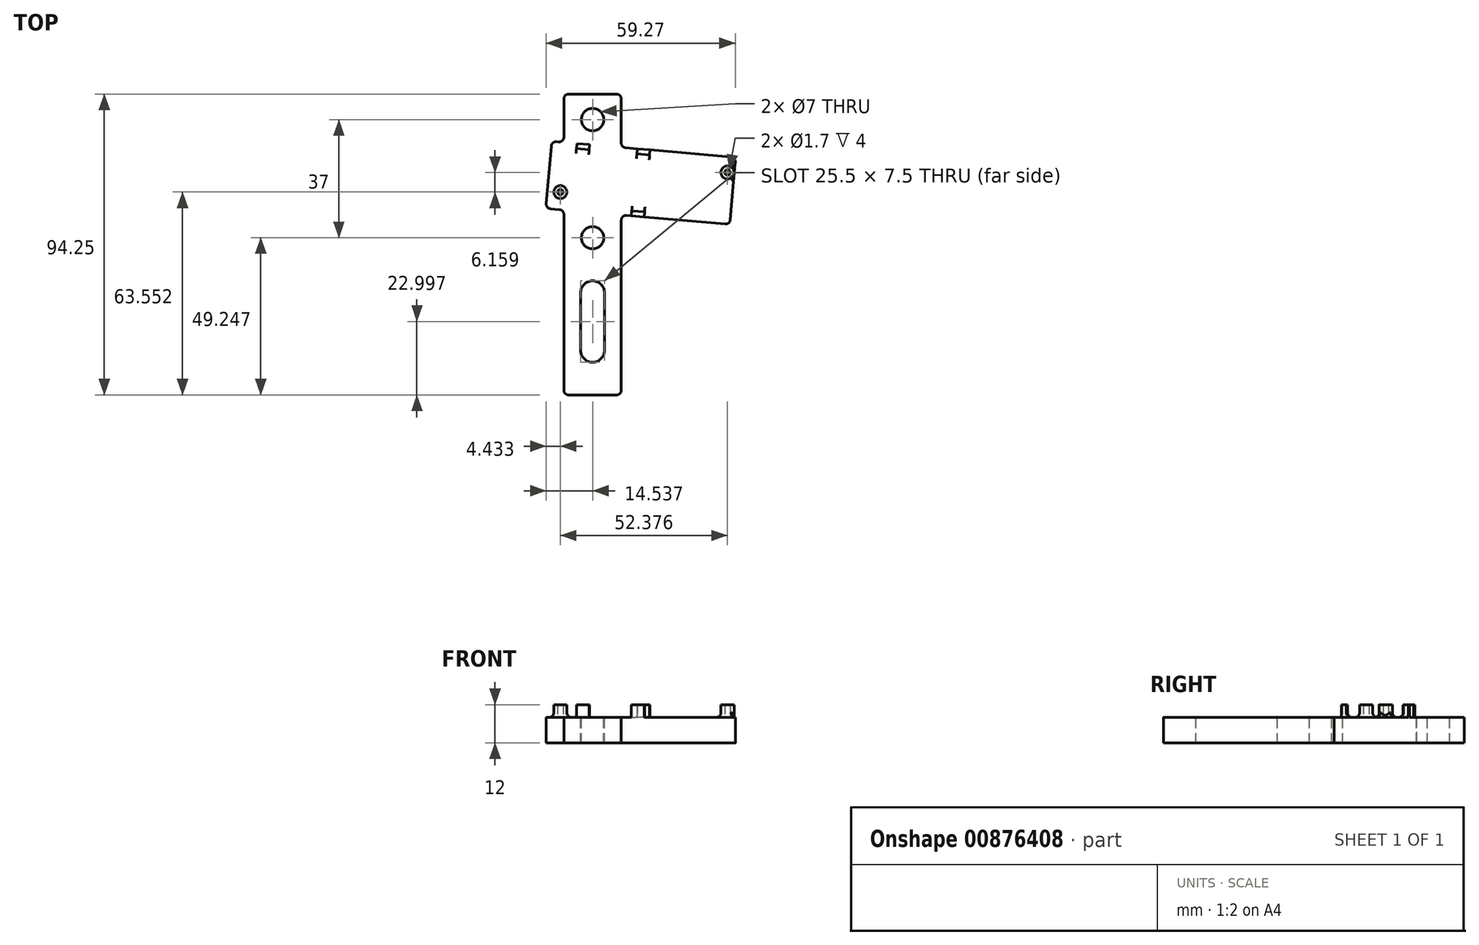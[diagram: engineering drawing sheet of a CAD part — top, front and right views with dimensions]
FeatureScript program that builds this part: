
annotation { "Feature Type Name" : "Feature", "Feature Type Description" : "" }
export const myFeature = defineFeature(function(context is Context, id is Id, definition is map)
    precondition{}
    {
        {
            var Q0;
            Q0=qCreatedBy(makeId("Top.planeOp"),FACE);
            var sketch = newSketch(context, id + "F0", { "sketchPlane" : qUnion([Q0])});
            skLineSegment(sketch, "E0", {"start": v(-42.89, -38.68) * mm, "end": v(35.48, -38.68) * mm, "construction": true});
            skCircle(sketch, "E1", {"center": v(-16.47, 2.12) * mm, "radius": 2.05 * mm});
            skCircle(sketch, "E2", {"center": v(35.9, 8.28) * mm, "radius": 2.05 * mm});
            skCircle(sketch, "E3", {"center": v(-16.47, 2.12) * mm, "radius": 0.85 * mm});
            skCircle(sketch, "E4", {"center": v(35.9, 8.28) * mm, "radius": 0.85 * mm});
            skLineSegment(sketch, "E5", {"start": v(-19.76, 11.54) * mm, "end": v(-9.28, 17.15) * mm, "construction": true});
            skLineSegment(sketch, "E6", {"start": v(-20.56, 2.34) * mm, "end": v(-11.12, -3.85) * mm, "construction": true});
            skLineSegment(sketch, "E7", {"start": v(28.2, -7.29) * mm, "end": v(37, -4.14) * mm, "construction": true});
            skLineSegment(sketch, "E8", {"start": v(-20.56, 2.34) * mm, "end": v(-21.03, -2.98) * mm, "construction": true});
            skLineSegment(sketch, "E9", {"start": v(-21.03, -2.98) * mm, "end": v(-11.12, -3.85) * mm, "construction": true});
            skLineSegment(sketch, "E10", {"start": v(-9.28, 17.15) * mm, "end": v(-19.2, 18.02) * mm, "construction": true});
            skLineSegment(sketch, "E11", {"start": v(-19.2, 18.02) * mm, "end": v(-19.76, 11.54) * mm, "construction": true});
            skLineSegment(sketch, "E12", {"start": v(37, -4.14) * mm, "end": v(36.66, -8.03) * mm, "construction": true});
            skLineSegment(sketch, "E13", {"start": v(36.66, -8.03) * mm, "end": v(28.2, -7.29) * mm, "construction": true});
            skLineSegment(sketch, "E14.bottom", {"start": v(11.5, 13.73) * mm, "end": v(11.65, 15.32) * mm});
            skLineSegment(sketch, "E14.top", {"start": v(7.52, 14.08) * mm, "end": v(7.66, 15.67) * mm});
            skLineSegment(sketch, "E14.left", {"start": v(11.5, 13.73) * mm, "end": v(7.52, 14.08) * mm});
            skLineSegment(sketch, "E14.right", {"start": v(11.65, 15.32) * mm, "end": v(7.66, 15.67) * mm});
            skLineSegment(sketch, "E15.bottom", {"start": v(9.76, -5.67) * mm, "end": v(9.9, -4.08) * mm});
            skLineSegment(sketch, "E15.top", {"start": v(5.78, -5.33) * mm, "end": v(5.92, -3.73) * mm});
            skLineSegment(sketch, "E15.left", {"start": v(9.76, -5.67) * mm, "end": v(5.78, -5.33) * mm});
            skLineSegment(sketch, "E15.right", {"start": v(9.9, -4.08) * mm, "end": v(5.92, -3.73) * mm});
            skPoint(sketch, "E16", {"position": v(9.65, 15.5) * mm});
            skPoint(sketch, "E17", {"position": v(7.82, -5.5) * mm});
            skPoint(sketch, "E18", {"position": v(-11.12, -3.85) * mm});
            skLineSegment(sketch, "E19.bottom", {"start": v(-11.41, 15.73) * mm, "end": v(-11.27, 17.33) * mm});
            skLineSegment(sketch, "E19.top", {"start": v(-7.43, 15.38) * mm, "end": v(-7.29, 16.98) * mm});
            skLineSegment(sketch, "E19.left", {"start": v(-11.41, 15.73) * mm, "end": v(-7.43, 15.38) * mm});
            skLineSegment(sketch, "E19.right", {"start": v(-11.27, 17.33) * mm, "end": v(-7.29, 16.98) * mm});
            skPoint(sketch, "E20", {"position": v(-9.28, 17.15) * mm});
            skLineSegment(sketch, "E21.bottom", {"start": v(-19.2, 18.02) * mm, "end": v(38.5, 12.97) * mm});
            skLineSegment(sketch, "E21.top", {"start": v(-21.03, -2.98) * mm, "end": v(36.66, -8.03) * mm});
            skLineSegment(sketch, "E21.left", {"start": v(-19.2, 18.02) * mm, "end": v(-21.03, -2.98) * mm});
            skLineSegment(sketch, "E21.right", {"start": v(38.5, 12.97) * mm, "end": v(36.66, -8.03) * mm});
            skLineSegment(sketch, "E22", {"start": v(-6.14, 8.8) * mm, "end": v(-6.58, 3.83) * mm, "construction": true});
            skPoint(sketch, "E23", {"position": v(-16.07, -3.41) * mm});
            skPoint(sketch, "E24", {"position": v(37.58, 2.47) * mm});
            skCircle(sketch, "E25.0", {"center": v(-6.36, -38.43) * mm, "radius": 3.75 * mm, "construction": true});
            skLineSegment(sketch, "E26.top", {"start": v(-15.36, -61.43) * mm, "end": v(2.64, -61.43) * mm});
            skLineSegment(sketch, "E26.left", {"start": v(-15.36, -3.48) * mm, "end": v(-15.36, -61.43) * mm});
            skLineSegment(sketch, "E26.right", {"start": v(2.64, -5.05) * mm, "end": v(2.64, -61.43) * mm});
            skLineSegment(sketch, "E27", {"start": v(-8.85, 6.54) * mm, "end": v(-3.87, 6.1) * mm, "construction": true});
            skPoint(sketch, "E28", {"position": v(-20.11, 7.52) * mm});
            skPoint(sketch, "E29", {"position": v(-6.36, 6.32) * mm});
            skArc(sketch, "E30", {"start": v(-2.61, -29.43) * mm, "mid": v(-6.36, -25.68) * mm, "end": v(-10.11, -29.43) * mm});
            skArc(sketch, "E31", {"start": v(-10.11, -47.43) * mm, "mid": v(-6.36, -51.18) * mm, "end": v(-2.61, -47.43) * mm});
            skLineSegment(sketch, "E32", {"start": v(-2.61, -29.43) * mm, "end": v(-2.61, -47.43) * mm});
            skLineSegment(sketch, "E33", {"start": v(-10.11, -29.43) * mm, "end": v(-10.11, -47.43) * mm});
            skCircle(sketch, "E34", {"center": v(-6.36, -12.18) * mm, "radius": 3.5 * mm});
            skCircle(sketch, "E35", {"center": v(-6.36, 24.82) * mm, "radius": 3.5 * mm});
            skLineSegment(sketch, "E36", {"start": v(2.64, 16.11) * mm, "end": v(2.64, 32.82) * mm});
            skLineSegment(sketch, "E37", {"start": v(2.64, 32.82) * mm, "end": v(-15.36, 32.82) * mm});
            skLineSegment(sketch, "E38", {"start": v(-15.36, 32.82) * mm, "end": v(-15.36, 17.68) * mm});
            skSolve(sketch);
        }
        {
            var Q0;
            Q0=makeQuery(id+"F0.imprint","IMPRINT",FACE,{"disambiguationData":[TD([[makeQuery(id+"F0.imprint","IMPRINT",EDGE,{"derivedFrom":sQuery(id+"F0.wireOp",EDGE,"E1")}),-1.0]])]});
            var Q1;
            {var subQ1=sQuery(id+"F0.wireOp",EDGE,"E19.right");Q1=makeQuery(id+"F0.imprint","IMPRINT",FACE,{"disambiguationData":[TD([[makeQuery(id+"F0.imprint","IMPRINT",EDGE,{"derivedFrom":subQ1}),1.0]])]});}
            var Q2;
            Q2=makeQuery(id+"F0.imprint","IMPRINT",FACE,{"disambiguationData":[TD([[makeQuery(id+"F0.imprint","IMPRINT",EDGE,{"derivedFrom":sQuery(id+"F0.wireOp",EDGE,"E26.top")}),1.0]])]});
            var Q3;
            Q3=makeQuery(id+"F0.imprint","IMPRINT",FACE,{"disambiguationData":[TD([[makeQuery(id+"F0.imprint","IMPRINT",EDGE,{"derivedFrom":sQuery(id+"F0.wireOp",EDGE,"E1")}),1.0]])]});
            var Q4;
            Q4=makeQuery(id+"F0.imprint","IMPRINT",FACE,{"disambiguationData":[TD([[makeQuery(id+"F0.imprint","IMPRINT",EDGE,{"derivedFrom":sQuery(id+"F0.wireOp",EDGE,"E3")}),1.0]])]});
            var Q5;
            Q5=makeQuery(id+"F0.imprint","IMPRINT",FACE,{"disambiguationData":[TD([[makeQuery(id+"F0.imprint","IMPRINT",EDGE,{"derivedFrom":sQuery(id+"F0.wireOp",EDGE,"E15.bottom")}),1.0]])]});
            var Q6;
            Q6=makeQuery(id+"F0.imprint","IMPRINT",FACE,{"disambiguationData":[TD([[makeQuery(id+"F0.imprint","IMPRINT",EDGE,{"derivedFrom":sQuery(id+"F0.wireOp",EDGE,"E2")}),1.0]])]});
            var Q7;
            Q7=makeQuery(id+"F0.imprint","IMPRINT",FACE,{"disambiguationData":[TD([[makeQuery(id+"F0.imprint","IMPRINT",EDGE,{"derivedFrom":sQuery(id+"F0.wireOp",EDGE,"E4")}),1.0]])]});
            var Q8;
            Q8=makeQuery(id+"F0.imprint","IMPRINT",FACE,{"disambiguationData":[TD([[makeQuery(id+"F0.imprint","IMPRINT",EDGE,{"derivedFrom":sQuery(id+"F0.wireOp",EDGE,"E14.bottom")}),1.0]])]});
            var Q9;
            Q9=makeQuery(id+"F0.imprint","IMPRINT",FACE,{"disambiguationData":[TD([[makeQuery(id+"F0.imprint","IMPRINT",EDGE,{"derivedFrom":sQuery(id+"F0.wireOp",EDGE,"E19.bottom")}),-1.0]])]});
            extrude(context, id + "F1", {"entities" : qUnion([Q0, Q1, Q2, Q3, Q4, Q5, Q6, Q7, Q8, Q9]), "oppositeDirection" : true, "depth" : 8 * mm, "offsetDistance" : 25 * mm});
        }
        {
            var Q0;
            Q0=makeQuery(id+"F0.imprint","IMPRINT",FACE,{"disambiguationData":[TD([[makeQuery(id+"F0.imprint","IMPRINT",EDGE,{"derivedFrom":sQuery(id+"F0.wireOp",EDGE,"E19.bottom")}),-1.0]])]});
            var Q1;
            Q1=makeQuery(id+"F0.imprint","IMPRINT",FACE,{"disambiguationData":[TD([[makeQuery(id+"F0.imprint","IMPRINT",EDGE,{"derivedFrom":sQuery(id+"F0.wireOp",EDGE,"E1")}),1.0]])]});
            var Q2;
            Q2=makeQuery(id+"F0.imprint","IMPRINT",FACE,{"disambiguationData":[TD([[makeQuery(id+"F0.imprint","IMPRINT",EDGE,{"derivedFrom":sQuery(id+"F0.wireOp",EDGE,"E14.bottom")}),1.0]])]});
            var Q3;
            Q3=makeQuery(id+"F0.imprint","IMPRINT",FACE,{"disambiguationData":[TD([[makeQuery(id+"F0.imprint","IMPRINT",EDGE,{"derivedFrom":sQuery(id+"F0.wireOp",EDGE,"E15.bottom")}),1.0]])]});
            var Q4;
            Q4=makeQuery(id+"F0.imprint","IMPRINT",FACE,{"disambiguationData":[TD([[makeQuery(id+"F0.imprint","IMPRINT",EDGE,{"derivedFrom":sQuery(id+"F0.wireOp",EDGE,"E2")}),1.0]])]});
            extrude(context, id + "F2", {"entities" : qUnion([Q0, Q1, Q2, Q3, Q4]), "operationType" : NewBodyOperationType.ADD, "depth" : 4 * mm, "offsetDistance" : 25 * mm});
        }
        {
            var Q0;
            Q0=makeQuery(id+"F2.opExtrude","CAP_EDGE",EDGE,{"disambiguationData":[OSD([sQuery(id+"F0.wireOp",EDGE,"E2")])],"isStart":true});
            var Q1;
            Q1=makeQuery(id+"F2.opExtrude","CAP_EDGE",EDGE,{"disambiguationData":[OSD([sQuery(id+"F0.wireOp",EDGE,"E15.right")])],"isStart":true});
            var Q2;
            Q2=makeQuery(id+"F2.opExtrude","CAP_EDGE",EDGE,{"disambiguationData":[OSD([sQuery(id+"F0.wireOp",EDGE,"E14.left")])],"isStart":true});
            var Q3;
            Q3=makeQuery(id+"F2.opExtrude","CAP_EDGE",EDGE,{"disambiguationData":[OSD([sQuery(id+"F0.wireOp",EDGE,"E19.left")])],"isStart":true});
            var Q4;
            Q4=makeQuery(id+"F2.opExtrude","CAP_EDGE",EDGE,{"disambiguationData":[OSD([sQuery(id+"F0.wireOp",EDGE,"E1")])],"isStart":true});
            fillet(context, id + "F3", {"entities" : qUnion([Q0, Q1, Q2, Q3, Q4]), "tangentPropagation" : true, "radius" : 1.5 * mm, "defaultsChanged" : true, "vertexSettings" : [], "allowEdgeOverflow" : false});
        }
        {
            var Q0;
            Q0=makeQuery(id+"F1.opExtrude","SWEPT_EDGE",EDGE,{"disambiguationData":[OSD([sQuery(id+"F0.wireOp",EDGE,"E26.top"),sQuery(id+"F0.wireOp",EDGE,"E26.right")])]});
            var Q1;
            Q1=makeQuery(id+"F1.opExtrude","SWEPT_EDGE",EDGE,{"disambiguationData":[OSD([sQuery(id+"F0.wireOp",EDGE,"E26.top"),sQuery(id+"F0.wireOp",EDGE,"E26.left")])]});
            var Q2;
            Q2=makeQuery(id+"F1.opExtrude","SWEPT_EDGE",EDGE,{"disambiguationData":[OSD([sQuery(id+"F0.wireOp",EDGE,"E21.top"),sQuery(id+"F0.wireOp",EDGE,"E21.right")])]});
            var Q3;
            Q3=makeQuery(id+"F1.opExtrude","SWEPT_EDGE",EDGE,{"disambiguationData":[OSD([sQuery(id+"F0.wireOp",EDGE,"E21.top"),sQuery(id+"F0.wireOp",EDGE,"E21.left")])]});
            var Q4;
            Q4=makeQuery(id+"F1.opExtrude","SWEPT_EDGE",EDGE,{"disambiguationData":[OSD([sQuery(id+"F0.wireOp",EDGE,"E21.bottom"),sQuery(id+"F0.wireOp",EDGE,"E21.left")])]});
            var Q5;
            Q5=makeQuery(id+"F1.opExtrude","SWEPT_EDGE",EDGE,{"disambiguationData":[OSD([sQuery(id+"F0.wireOp",EDGE,"E37"),sQuery(id+"F0.wireOp",EDGE,"E38")])]});
            var Q6;
            Q6=makeQuery(id+"F1.opExtrude","SWEPT_EDGE",EDGE,{"disambiguationData":[OSD([sQuery(id+"F0.wireOp",EDGE,"E36"),sQuery(id+"F0.wireOp",EDGE,"E37")])]});
            var Q7;
            Q7=makeQuery(id+"F1.opExtrude","SWEPT_EDGE",EDGE,{"disambiguationData":[OSD([sQuery(id+"F0.wireOp",EDGE,"E21.bottom"),sQuery(id+"F0.wireOp",EDGE,"E21.right")])]});
            var Q8;
            Q8=makeQuery(id+"F1.opExtrude","SWEPT_EDGE",EDGE,{"disambiguationData":[OSD([sQuery(id+"F0.wireOp",EDGE,"E21.bottom"),sQuery(id+"F0.wireOp",EDGE,"E36")])]});
            var Q9;
            Q9=makeQuery(id+"F1.opExtrude","SWEPT_EDGE",EDGE,{"disambiguationData":[OSD([sQuery(id+"F0.wireOp",EDGE,"E21.bottom"),sQuery(id+"F0.wireOp",EDGE,"E38")])]});
            var Q10;
            Q10=makeQuery(id+"F1.opExtrude","SWEPT_EDGE",EDGE,{"disambiguationData":[OSD([sQuery(id+"F0.wireOp",EDGE,"E21.top"),sQuery(id+"F0.wireOp",EDGE,"E26.left")])]});
            var Q11;
            Q11=makeQuery(id+"F1.opExtrude","SWEPT_EDGE",EDGE,{"disambiguationData":[OSD([sQuery(id+"F0.wireOp",EDGE,"E21.top"),sQuery(id+"F0.wireOp",EDGE,"E26.right")])]});
            fillet(context, id + "F4", {"entities" : qUnion([Q0, Q1, Q2, Q3, Q4, Q5, Q6, Q7, Q8, Q9, Q10, Q11]), "tangentPropagation" : true, "radius" : 1.5 * mm, "defaultsChanged" : true, "vertexSettings" : [], "allowEdgeOverflow" : false});
        }
    });
